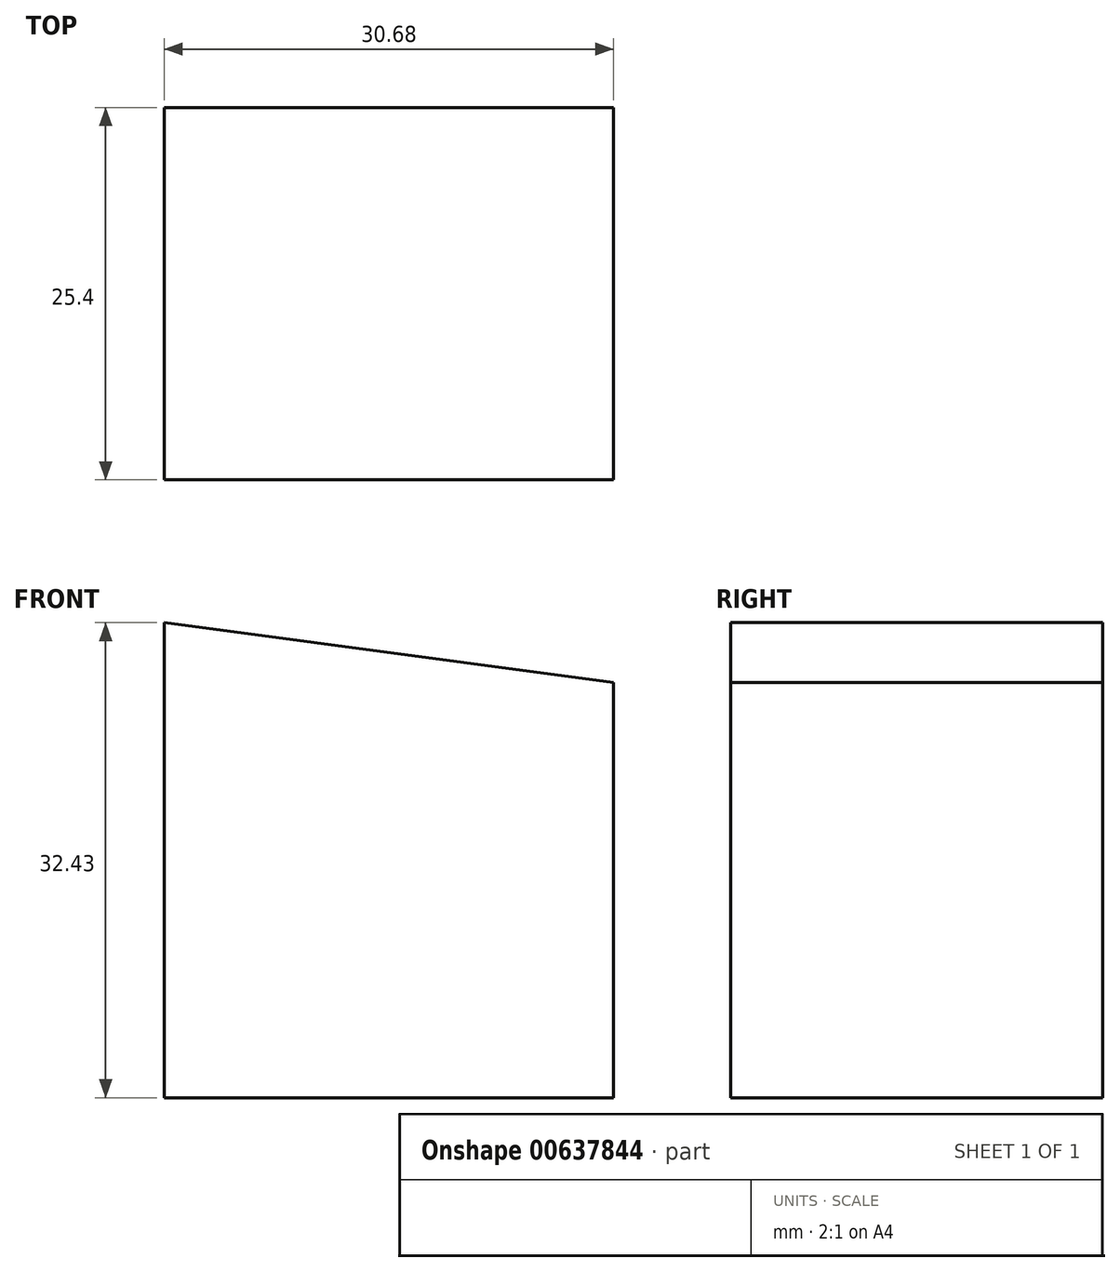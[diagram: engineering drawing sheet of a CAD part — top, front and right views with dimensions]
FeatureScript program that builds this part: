
annotation { "Feature Type Name" : "Feature", "Feature Type Description" : "" }
export const myFeature = defineFeature(function(context is Context, id is Id, definition is map)
    precondition{}
    {
        {
            var Q0;
            Q0=qCreatedBy(makeId("Front.planeOp"),FACE);
            var sketch = newSketch(context, id + "F0", { "sketchPlane" : qUnion([Q0])});
            skLineSegment(sketch, "E0", {"start": v(-57.07, 51.85) * mm, "end": v(-57.07, 19.42) * mm});
            skLineSegment(sketch, "E1", {"start": v(-57.07, 19.42) * mm, "end": v(-26.4, 19.42) * mm});
            skLineSegment(sketch, "E2", {"start": v(-26.4, 19.42) * mm, "end": v(-26.4, 47.76) * mm});
            skLineSegment(sketch, "E3", {"start": v(-26.4, 47.76) * mm, "end": v(-57.07, 51.85) * mm});
            skSolve(sketch);
        }
        {
            var Q0;
            Q0 = qSketchRegion(id + "F0", true);
            extrude(context, id + "F1", {"entities" : qUnion([Q0]), "depth" : 25.4 * mm, "offsetDistance" : 25.4 * mm});
        }
    });
